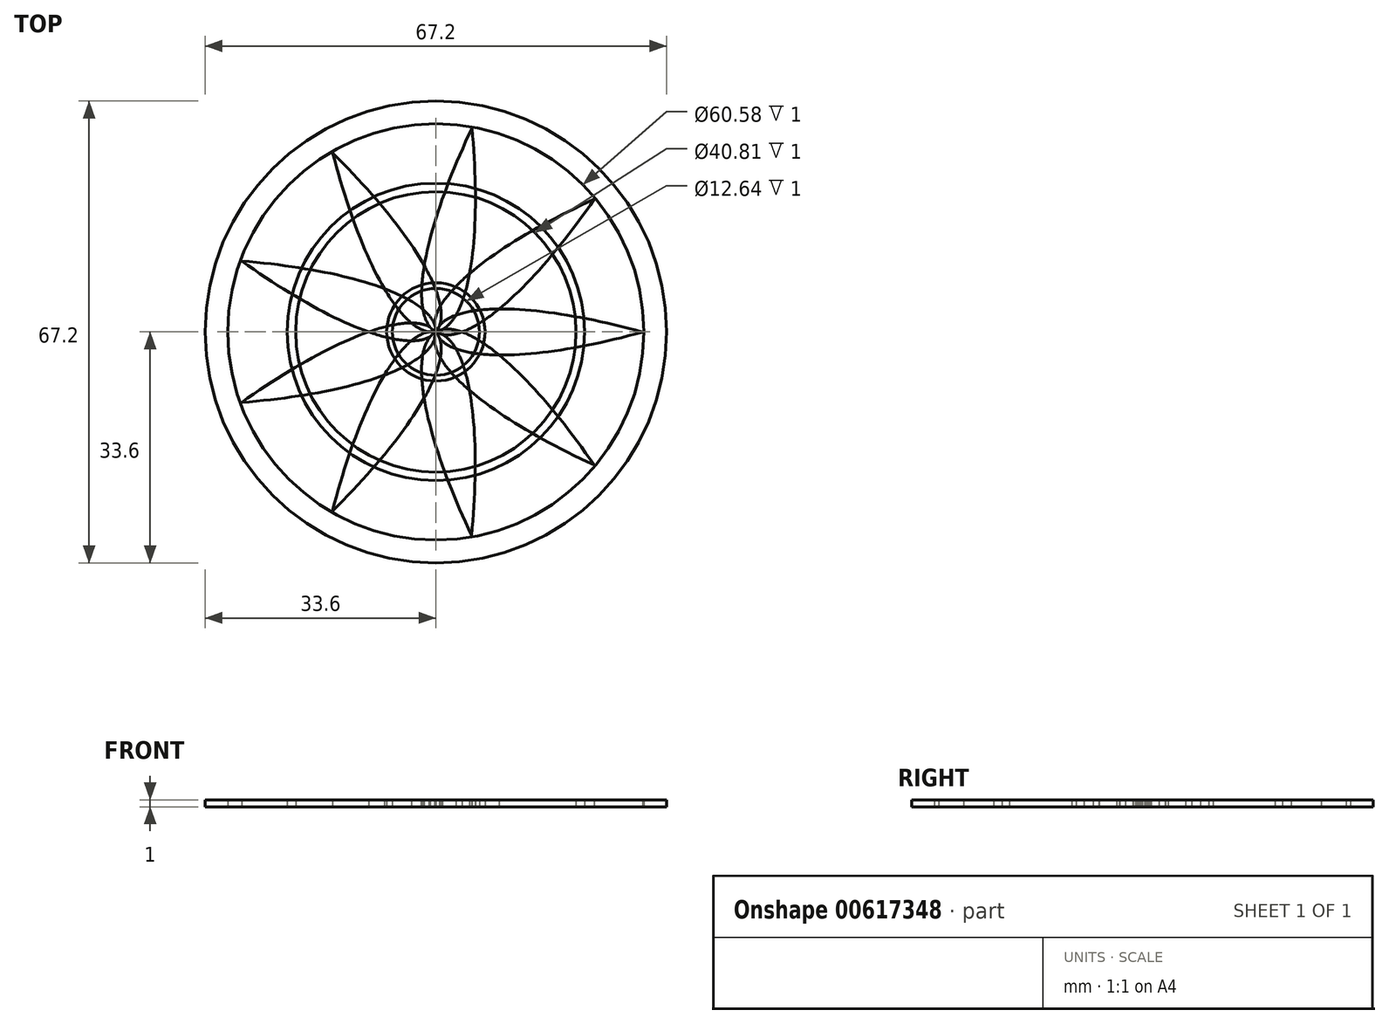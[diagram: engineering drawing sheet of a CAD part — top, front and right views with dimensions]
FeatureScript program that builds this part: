
annotation { "Feature Type Name" : "Feature", "Feature Type Description" : "" }
export const myFeature = defineFeature(function(context is Context, id is Id, definition is map)
    precondition{}
    {
        {
            var Q0;
            Q0=qCreatedBy(makeId("Top.planeOp"),FACE);
            var sketch = newSketch(context, id + "F0", { "sketchPlane" : qUnion([Q0])});
            skEllipse(sketch, "E0", {"center": v(-30.18, 25.36) * mm, "majorRadius": 39.42 * mm, "minorRadius": 10.73 * mm, "majorAxis": v(0.77, -0.64)});
            skEllipse(sketch, "E1.1.0", {"center": v(-39.42, 0.03) * mm, "majorRadius": 39.42 * mm, "minorRadius": 10.73 * mm, "majorAxis": v(1, 0)});
            skEllipse(sketch, "E1.2.0", {"center": v(-30.22, -25.31) * mm, "majorRadius": 39.42 * mm, "minorRadius": 10.73 * mm, "majorAxis": v(0.77, 0.64)});
            skEllipse(sketch, "E1.3.0", {"center": v(-6.88, -38.81) * mm, "majorRadius": 39.42 * mm, "minorRadius": 10.73 * mm, "majorAxis": v(0.17, 0.98)});
            skEllipse(sketch, "E1.4.0", {"center": v(19.68, -34.15) * mm, "majorRadius": 39.42 * mm, "minorRadius": 10.73 * mm, "majorAxis": v(-0.5, 0.87)});
            skEllipse(sketch, "E1.5.0", {"center": v(37.03, -13.51) * mm, "majorRadius": 39.42 * mm, "minorRadius": 10.73 * mm, "majorAxis": v(-0.94, 0.34)});
            skEllipse(sketch, "E1.6.0", {"center": v(37.05, 13.45) * mm, "majorRadius": 39.42 * mm, "minorRadius": 10.73 * mm, "majorAxis": v(-0.94, -0.34)});
            skEllipse(sketch, "E1.7.0", {"center": v(19.74, 34.12) * mm, "majorRadius": 39.42 * mm, "minorRadius": 10.73 * mm, "majorAxis": v(-0.5, -0.87)});
            skEllipse(sketch, "E1.8.0", {"center": v(-6.81, 38.82) * mm, "majorRadius": 39.42 * mm, "minorRadius": 10.73 * mm, "majorAxis": v(0.17, -0.98)});
            skPoint(sketch, "E1.center", {"position": v(0, 0) * mm});
            skSolve(sketch);
        }
        {
            var Q0;
            {var subQ0=sQuery(id+"F0.wireOp",EDGE,"E1.6.0");var subQ1=sQuery(id+"F0.wireOp",EDGE,"E1.1.0");var subQ2=makeQuery(id+"F0.imprint","INTERSECT",VERTEX,{"derivedFrom":[subQ1,subQ0]});Q0=makeQuery(id+"F0.imprint","IMPRINT",FACE,{"disambiguationData":[TD([[makeQuery(id+"F0.imprint","IMPRINT",EDGE,{"disambiguationData":[TD([[subQ2,-1.0]])],"derivedFrom":subQ1}),1.0]])]});}
            var Q1;
            {var subQ0=sQuery(id+"F0.wireOp",EDGE,"E1.5.0");var subQ1=sQuery(id+"F0.wireOp",EDGE,"E0");var subQ2=makeQuery(id+"F0.imprint","INTERSECT",VERTEX,{"derivedFrom":[subQ1,subQ0]});Q1=makeQuery(id+"F0.imprint","IMPRINT",FACE,{"disambiguationData":[TD([[makeQuery(id+"F0.imprint","IMPRINT",EDGE,{"disambiguationData":[TD([[subQ2,-1.0]])],"derivedFrom":subQ1}),1.0]])]});}
            var Q2;
            {var subQ0=sQuery(id+"F0.wireOp",EDGE,"E1.5.0");var subQ1=sQuery(id+"F0.wireOp",EDGE,"E0");var subQ2=makeQuery(id+"F0.imprint","INTERSECT",VERTEX,{"derivedFrom":[subQ1,subQ0]});Q2=makeQuery(id+"F0.imprint","IMPRINT",FACE,{"disambiguationData":[TD([[makeQuery(id+"F0.imprint","IMPRINT",EDGE,{"disambiguationData":[TD([[subQ2,1.0]])],"derivedFrom":subQ0}),1.0]])]});}
            var Q3;
            {var subQ0=sQuery(id+"F0.wireOp",EDGE,"E1.7.0");var subQ4=sQuery(id+"F0.wireOp",EDGE,"E1.4.0");var subQ6=makeQuery(id+"F0.imprint","INTERSECT",VERTEX,{"derivedFrom":[subQ4,subQ0]});Q3=makeQuery(id+"F0.imprint","IMPRINT",FACE,{"disambiguationData":[TD([[makeQuery(id+"F0.imprint","IMPRINT",EDGE,{"disambiguationData":[TD([[subQ6,-1.0]])],"derivedFrom":subQ4}),1.0]])]});}
            var Q4;
            {var subQ0=sQuery(id+"F0.wireOp",EDGE,"E1.6.0");var subQ4=sQuery(id+"F0.wireOp",EDGE,"E1.3.0");var subQ6=makeQuery(id+"F0.imprint","INTERSECT",VERTEX,{"derivedFrom":[subQ4,subQ0]});Q4=makeQuery(id+"F0.imprint","IMPRINT",FACE,{"disambiguationData":[TD([[makeQuery(id+"F0.imprint","IMPRINT",EDGE,{"disambiguationData":[TD([[subQ6,-1.0]])],"derivedFrom":subQ4}),1.0]])]});}
            var Q5;
            {var subQ0=sQuery(id+"F0.wireOp",EDGE,"E1.5.0");var subQ4=sQuery(id+"F0.wireOp",EDGE,"E1.2.0");var subQ6=makeQuery(id+"F0.imprint","INTERSECT",VERTEX,{"derivedFrom":[subQ4,subQ0]});Q5=makeQuery(id+"F0.imprint","IMPRINT",FACE,{"disambiguationData":[TD([[makeQuery(id+"F0.imprint","IMPRINT",EDGE,{"disambiguationData":[TD([[subQ6,-1.0]])],"derivedFrom":subQ4}),1.0]])]});}
            var Q6;
            {var subQ0=sQuery(id+"F0.wireOp",EDGE,"E1.4.0");var subQ4=sQuery(id+"F0.wireOp",EDGE,"E1.1.0");var subQ6=makeQuery(id+"F0.imprint","INTERSECT",VERTEX,{"derivedFrom":[subQ4,subQ0]});Q6=makeQuery(id+"F0.imprint","IMPRINT",FACE,{"disambiguationData":[TD([[makeQuery(id+"F0.imprint","IMPRINT",EDGE,{"disambiguationData":[TD([[subQ6,-1.0]])],"derivedFrom":subQ4}),1.0]])]});}
            var Q7;
            {var subQ0=sQuery(id+"F0.wireOp",EDGE,"E1.3.0");var subQ1=sQuery(id+"F0.wireOp",EDGE,"E0");var subQ2=makeQuery(id+"F0.imprint","INTERSECT",VERTEX,{"derivedFrom":[subQ1,subQ0]});Q7=makeQuery(id+"F0.imprint","IMPRINT",FACE,{"disambiguationData":[TD([[makeQuery(id+"F0.imprint","IMPRINT",EDGE,{"disambiguationData":[TD([[subQ2,-1.0]])],"derivedFrom":subQ1}),1.0]])]});}
            var Q8;
            {var subQ0=sQuery(id+"F0.wireOp",EDGE,"E1.7.0");var subQ1=sQuery(id+"F0.wireOp",EDGE,"E1.2.0");var subQ2=makeQuery(id+"F0.imprint","INTERSECT",VERTEX,{"derivedFrom":[subQ1,subQ0]});Q8=makeQuery(id+"F0.imprint","IMPRINT",FACE,{"disambiguationData":[TD([[makeQuery(id+"F0.imprint","IMPRINT",EDGE,{"disambiguationData":[TD([[subQ2,-1.0]])],"derivedFrom":subQ1}),1.0]])]});}
            extrude(context, id + "F1", {"entities" : qUnion([Q0, Q1, Q2, Q3, Q4, Q5, Q6, Q7, Q8]), "depth" : 1 * mm, "offsetDistance" : 25 * mm});
        }
        {
            var Q0;
            {var subQ0=sQuery(id+"F0.wireOp",EDGE,"E1.8.0");var subQ1=sQuery(id+"F0.wireOp",EDGE,"E0");var subQ2=makeQuery(id+"F0.imprint","INTERSECT",VERTEX,{"derivedFrom":[subQ1,subQ0]});Q0=makeQuery(id+"F0.imprint","IMPRINT",FACE,{"disambiguationData":[TD([[makeQuery(id+"F0.imprint","IMPRINT",EDGE,{"disambiguationData":[TD([[subQ2,1.0]])],"derivedFrom":subQ1}),1.0]])]});}
            var Q1;
            {var subQ0=sQuery(id+"F0.wireOp",EDGE,"E1.6.0");var subQ1=sQuery(id+"F0.wireOp",EDGE,"E0");var subQ2=makeQuery(id+"F0.imprint","INTERSECT",VERTEX,{"derivedFrom":[subQ1,subQ0]});Q1=makeQuery(id+"F0.imprint","IMPRINT",FACE,{"disambiguationData":[TD([[makeQuery(id+"F0.imprint","IMPRINT",EDGE,{"disambiguationData":[TD([[subQ2,-1.0]])],"derivedFrom":subQ1}),-1.0]])]});}
            var Q2;
            {var subQ0=sQuery(id+"F0.wireOp",EDGE,"E1.7.0");var subQ1=sQuery(id+"F0.wireOp",EDGE,"E1.5.0");var subQ2=makeQuery(id+"F0.imprint","INTERSECT",VERTEX,{"derivedFrom":[subQ1,subQ0]});Q2=makeQuery(id+"F0.imprint","IMPRINT",FACE,{"disambiguationData":[TD([[makeQuery(id+"F0.imprint","IMPRINT",EDGE,{"disambiguationData":[TD([[subQ2,-1.0]])],"derivedFrom":subQ1}),-1.0]])]});}
            var Q3;
            {var subQ0=sQuery(id+"F0.wireOp",EDGE,"E1.6.0");var subQ1=sQuery(id+"F0.wireOp",EDGE,"E1.4.0");var subQ2=makeQuery(id+"F0.imprint","INTERSECT",VERTEX,{"derivedFrom":[subQ1,subQ0]});Q3=makeQuery(id+"F0.imprint","IMPRINT",FACE,{"disambiguationData":[TD([[makeQuery(id+"F0.imprint","IMPRINT",EDGE,{"disambiguationData":[TD([[subQ2,-1.0]])],"derivedFrom":subQ1}),-1.0]])]});}
            var Q4;
            {var subQ0=sQuery(id+"F0.wireOp",EDGE,"E1.5.0");var subQ1=sQuery(id+"F0.wireOp",EDGE,"E1.3.0");var subQ2=makeQuery(id+"F0.imprint","INTERSECT",VERTEX,{"derivedFrom":[subQ1,subQ0]});Q4=makeQuery(id+"F0.imprint","IMPRINT",FACE,{"disambiguationData":[TD([[makeQuery(id+"F0.imprint","IMPRINT",EDGE,{"disambiguationData":[TD([[subQ2,-1.0]])],"derivedFrom":subQ1}),-1.0]])]});}
            var Q5;
            {var subQ0=sQuery(id+"F0.wireOp",EDGE,"E1.4.0");var subQ1=sQuery(id+"F0.wireOp",EDGE,"E1.2.0");var subQ2=makeQuery(id+"F0.imprint","INTERSECT",VERTEX,{"derivedFrom":[subQ1,subQ0]});Q5=makeQuery(id+"F0.imprint","IMPRINT",FACE,{"disambiguationData":[TD([[makeQuery(id+"F0.imprint","IMPRINT",EDGE,{"disambiguationData":[TD([[subQ2,-1.0]])],"derivedFrom":subQ1}),-1.0]])]});}
            var Q6;
            {var subQ0=sQuery(id+"F0.wireOp",EDGE,"E1.3.0");var subQ1=sQuery(id+"F0.wireOp",EDGE,"E1.1.0");var subQ2=makeQuery(id+"F0.imprint","INTERSECT",VERTEX,{"derivedFrom":[subQ1,subQ0]});Q6=makeQuery(id+"F0.imprint","IMPRINT",FACE,{"disambiguationData":[TD([[makeQuery(id+"F0.imprint","IMPRINT",EDGE,{"disambiguationData":[TD([[subQ2,-1.0]])],"derivedFrom":subQ1}),-1.0]])]});}
            var Q7;
            {var subQ0=sQuery(id+"F0.wireOp",EDGE,"E1.2.0");var subQ1=sQuery(id+"F0.wireOp",EDGE,"E0");var subQ2=makeQuery(id+"F0.imprint","INTERSECT",VERTEX,{"derivedFrom":[subQ1,subQ0]});Q7=makeQuery(id+"F0.imprint","IMPRINT",FACE,{"disambiguationData":[TD([[makeQuery(id+"F0.imprint","IMPRINT",EDGE,{"disambiguationData":[TD([[subQ2,-1.0]])],"derivedFrom":subQ1}),-1.0]])]});}
            var Q8;
            {var subQ0=sQuery(id+"F0.wireOp",EDGE,"E1.1.0");var subQ1=sQuery(id+"F0.wireOp",EDGE,"E0");var subQ2=makeQuery(id+"F0.imprint","INTERSECT",VERTEX,{"derivedFrom":[subQ1,subQ0]});Q8=makeQuery(id+"F0.imprint","IMPRINT",FACE,{"disambiguationData":[TD([[makeQuery(id+"F0.imprint","IMPRINT",EDGE,{"disambiguationData":[TD([[subQ2,-1.0]])],"derivedFrom":subQ1}),1.0]])]});}
            extrude(context, id + "F2", {"entities" : qUnion([Q0, Q1, Q2, Q3, Q4, Q5, Q6, Q7, Q8]), "depth" : 1 * mm, "offsetDistance" : 25 * mm});
        }
        {
            var Q0;
            Q0=qCreatedBy(makeId("Top.planeOp"),FACE);
            var sketch = newSketch(context, id + "F3", { "sketchPlane" : qUnion([Q0])});
            skCircle(sketch, "E2", {"center": v(0, 0) * mm, "radius": 30.29 * mm});
            skCircle(sketch, "E3", {"center": v(0, 0) * mm, "radius": 33.6 * mm});
            skSolve(sketch);
        }
        {
            var Q0;
            Q0=qSketchRegion(id+"F3",true);
            extrude(context, id + "F4", {"entities" : qUnion([Q0]), "depth" : 1 * mm, "offsetDistance" : 25 * mm});
        }
        {
            var Q0;
            {var subQ0=sQuery(id+"F0.wireOp",EDGE,"E1.2.0");var subQ1=sQuery(id+"F0.wireOp",EDGE,"E1.1.0");var subQ2=makeQuery(id+"F0.imprint","INTERSECT",VERTEX,{"derivedFrom":[subQ1,subQ0]});Q0=makeQuery(id+"F0.imprint","IMPRINT",FACE,{"disambiguationData":[TD([[makeQuery(id+"F0.imprint","IMPRINT",EDGE,{"disambiguationData":[TD([[subQ2,-1.0]])],"derivedFrom":subQ1}),-1.0]])]});}
            var sketch = newSketch(context, id + "F5", { "sketchPlane" : qUnion([Q0])});
            skCircle(sketch, "E4", {"center": v(0, 0) * mm, "radius": 2.47 * mm});
            skCircle(sketch, "E5", {"center": v(0, 0) * mm, "radius": 3.2 * mm});
            skSolve(sketch);
        }
        {
            var Q0;
            Q0=sQuery(id+"F5.wireOp",EDGE,"E4");
            var Q1;
            Q1=sQuery(id+"F5.wireOp",EDGE,"E5");
            extrude(context, id + "F6", {"bodyType" : ToolBodyType.SURFACE, "surfaceEntities" : qUnion([Q0, Q1]), "depth" : 1 * mm, "offsetDistance" : 25 * mm});
        }
        {
            var Q0;
            Q0=makeQuery(id+"F3.imprint","IMPRINT",FACE,{"disambiguationData":[TD([[makeQuery(id+"F3.imprint","IMPRINT",EDGE,{"derivedFrom":sQuery(id+"F3.wireOp",EDGE,"E2")}),1.0]])]});
            var sketch = newSketch(context, id + "F7", { "sketchPlane" : qUnion([Q0])});
            skCircle(sketch, "E6", {"center": v(0, 0) * mm, "radius": 6.32 * mm});
            skCircle(sketch, "E7", {"center": v(0, 0) * mm, "radius": 7.15 * mm});
            skSolve(sketch);
        }
        {
            var Q0;
            Q0=qSketchRegion(id+"F7",true);
            extrude(context, id + "F8", {"entities" : qUnion([Q0]), "depth" : 1 * mm, "offsetDistance" : 25 * mm});
        }
        {
            var Q0;
            Q0=makeQuery(id+"F3.imprint","IMPRINT",FACE,{"disambiguationData":[TD([[makeQuery(id+"F3.imprint","IMPRINT",EDGE,{"derivedFrom":sQuery(id+"F3.wireOp",EDGE,"E2")}),1.0]])]});
            var sketch = newSketch(context, id + "F9", { "sketchPlane" : qUnion([Q0])});
            skCircle(sketch, "E8", {"center": v(0, 0) * mm, "radius": 20.4 * mm});
            skCircle(sketch, "E9", {"center": v(0, 0) * mm, "radius": 21.64 * mm});
            skSolve(sketch);
        }
        {
            var Q0;
            Q0=qSketchRegion(id+"F9",true);
            extrude(context, id + "F10", {"entities" : qUnion([Q0]), "depth" : 1 * mm, "offsetDistance" : 25 * mm});
        }
    });
